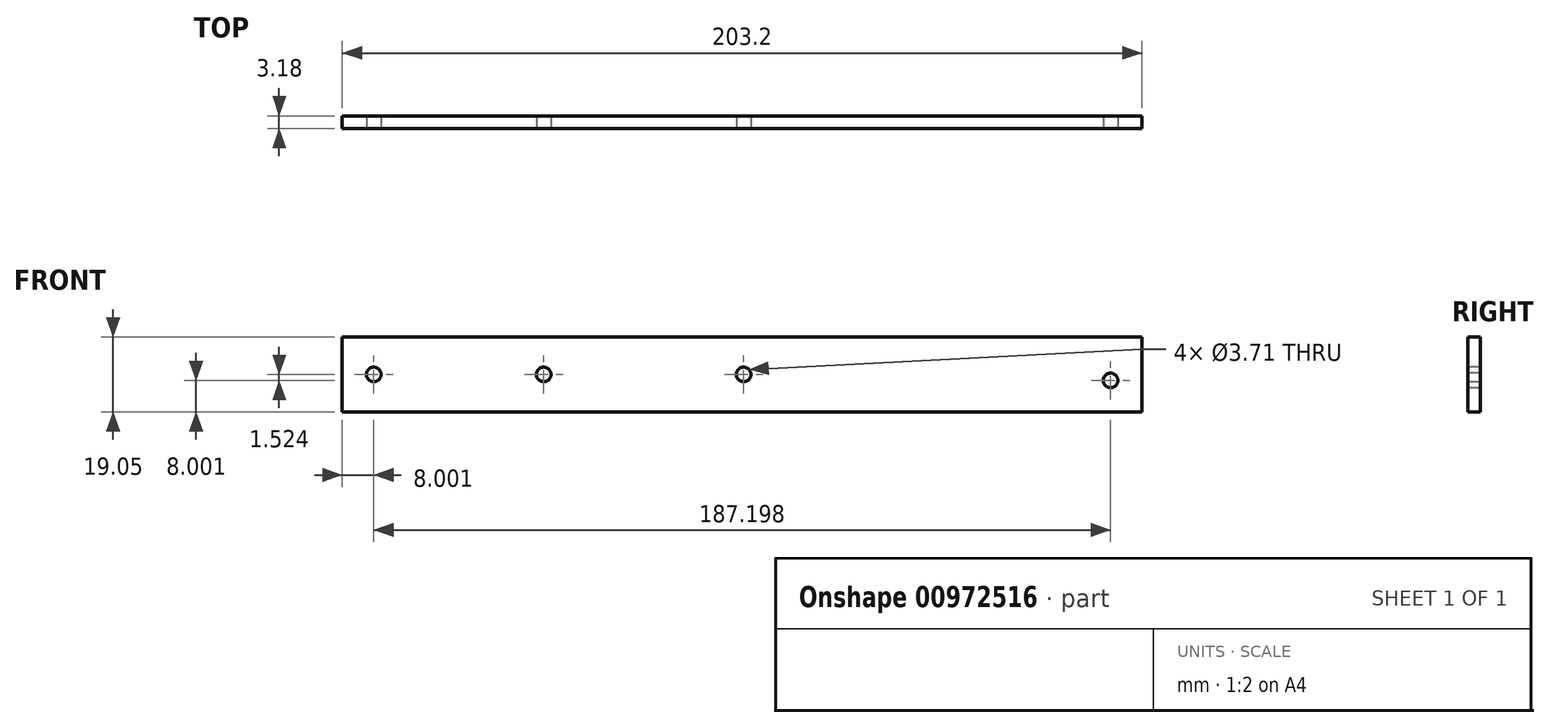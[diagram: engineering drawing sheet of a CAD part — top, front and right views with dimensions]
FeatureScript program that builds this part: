
annotation { "Feature Type Name" : "Feature", "Feature Type Description" : "" }
export const myFeature = defineFeature(function(context is Context, id is Id, definition is map)
    precondition{}
    {
        {
            var Q0;
            Q0=qCreatedBy(makeId("Front.planeOp"),FACE);
            var sketch = newSketch(context, id + "F0", { "sketchPlane" : qUnion([Q0])});
            skLineSegment(sketch, "E0.bottom", {"start": v(0, 0) * mm, "end": v(-203.2, 0) * mm});
            skLineSegment(sketch, "E0.top", {"start": v(0, 19.05) * mm, "end": v(-203.2, 19.05) * mm});
            skLineSegment(sketch, "E0.left", {"start": v(0, 0) * mm, "end": v(0, 19.05) * mm});
            skLineSegment(sketch, "E0.right", {"start": v(-203.2, 0) * mm, "end": v(-203.2, 19.05) * mm});
            skSolve(sketch);
        }
        {
            var Q0;
            Q0=makeQuery(id+"F0.imprint","IMPRINT",FACE,{"disambiguationData":[TD([[makeQuery(id+"F0.imprint","IMPRINT",EDGE,{"derivedFrom":sQuery(id+"F0.wireOp",EDGE,"E0.bottom")}),-1.0]])]});
            extrude(context, id + "F1", {"entities" : qUnion([Q0]), "depth" : 3.17 * mm, "offsetDistance" : 25.4 * mm});
        }
        {
            var Q0;
            Q0=makeQuery(id+"F1.opExtrude","CAP_FACE",FACE,{"disambiguationData":[OSD([sQuery(id+"F0.wireOp",EDGE,"E0.bottom"),sQuery(id+"F0.wireOp",EDGE,"E0.top"),sQuery(id+"F0.wireOp",EDGE,"E0.left"),sQuery(id+"F0.wireOp",EDGE,"E0.right")])],"isStart":false});
            var sketch = newSketch(context, id + "F2", { "sketchPlane" : qUnion([Q0])});
            skCircle(sketch, "E1", {"center": v(-195.2, 9.52) * mm, "radius": 1.86 * mm});
            skPoint(sketch, "E1.centerSnap0", {"position": v(-203.2, 9.52) * mm});
            skCircle(sketch, "E2", {"center": v(-8, 8) * mm, "radius": 1.86 * mm});
            skCircle(sketch, "E3", {"center": v(-152.02, 9.52) * mm, "radius": 1.86 * mm});
            skCircle(sketch, "E4", {"center": v(-101.22, 9.52) * mm, "radius": 1.86 * mm});
            skSolve(sketch);
        }
        {
            var Q0;
            Q0=makeQuery(id+"F2.imprint","IMPRINT",FACE,{"disambiguationData":[TD([[makeQuery(id+"F2.imprint","IMPRINT",EDGE,{"derivedFrom":sQuery(id+"F2.wireOp",EDGE,"E1")}),1.0]])]});
            var Q1;
            Q1=makeQuery(id+"F2.imprint","IMPRINT",FACE,{"disambiguationData":[TD([[makeQuery(id+"F2.imprint","IMPRINT",EDGE,{"derivedFrom":sQuery(id+"F2.wireOp",EDGE,"E3")}),1.0]])]});
            var Q2;
            Q2=makeQuery(id+"F2.imprint","IMPRINT",FACE,{"disambiguationData":[TD([[makeQuery(id+"F2.imprint","IMPRINT",EDGE,{"derivedFrom":sQuery(id+"F2.wireOp",EDGE,"E4")}),1.0]])]});
            var Q3;
            Q3=makeQuery(id+"F2.imprint","IMPRINT",FACE,{"disambiguationData":[TD([[makeQuery(id+"F2.imprint","IMPRINT",EDGE,{"derivedFrom":sQuery(id+"F2.wireOp",EDGE,"E2")}),1.0]])]});
            extrude(context, id + "F3", {"entities" : qUnion([Q0, Q1, Q2, Q3]), "operationType" : NewBodyOperationType.REMOVE, "oppositeDirection" : true, "depth" : 25.4 * mm, "offsetDistance" : 25.4 * mm});
        }
    });
